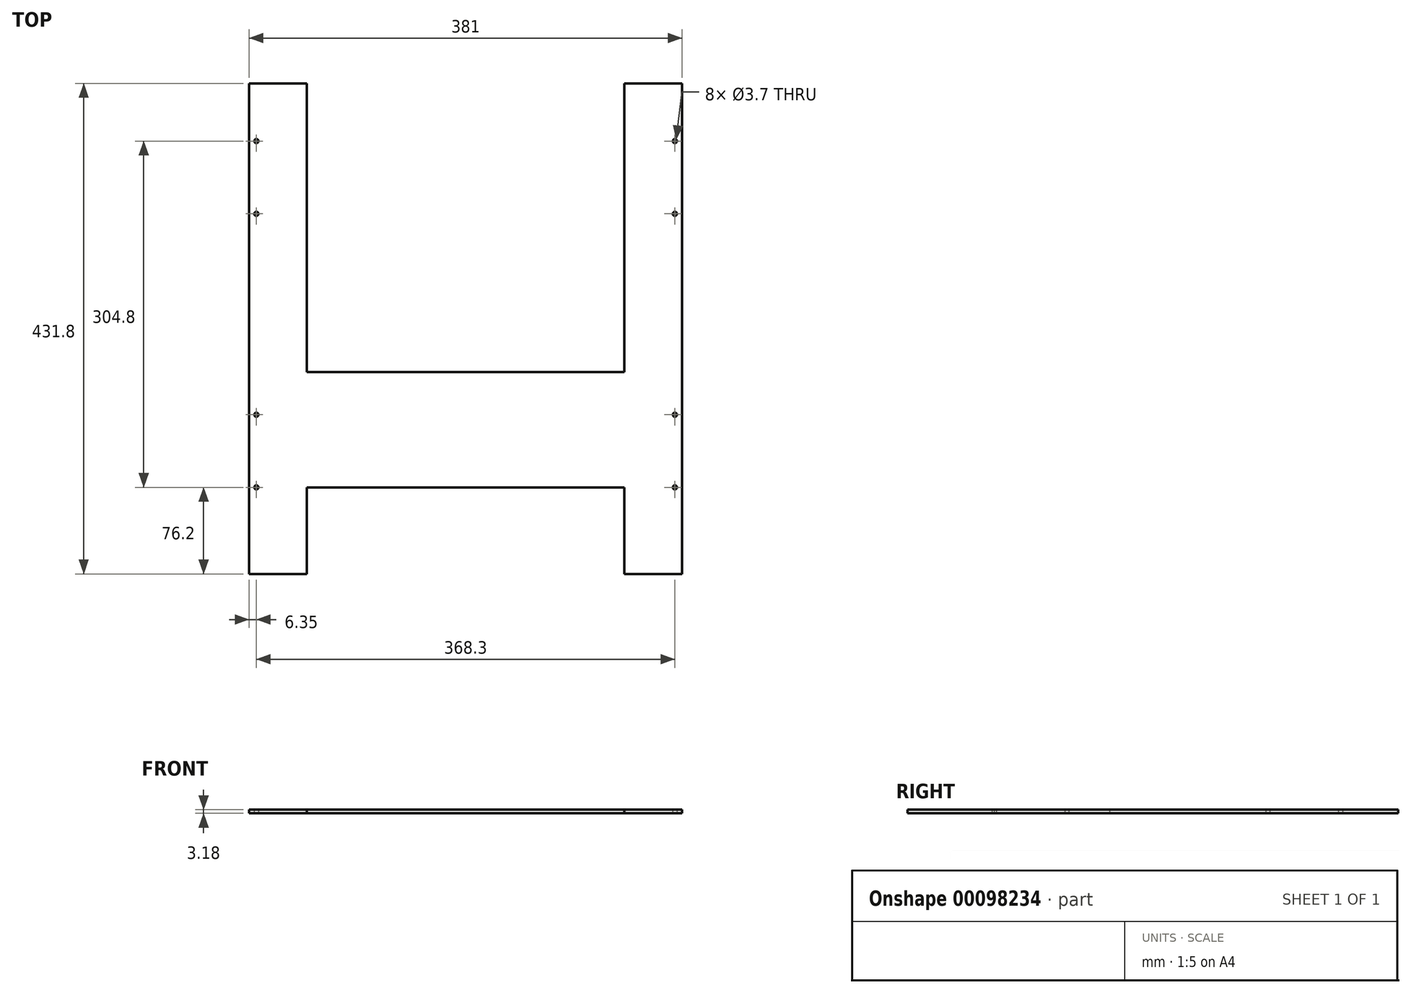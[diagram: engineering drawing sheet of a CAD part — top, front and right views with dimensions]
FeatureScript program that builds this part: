
annotation { "Feature Type Name" : "Feature", "Feature Type Description" : "" }
export const myFeature = defineFeature(function(context is Context, id is Id, definition is map)
    precondition{}
    {
        {
            var Q0;
            Q0=qCreatedBy(makeId("Top.planeOp"),FACE);
            var sketch = newSketch(context, id + "F0", { "sketchPlane" : qUnion([Q0])});
            skLineSegment(sketch, "E0.bottom", {"start": v(190.5, 215.9) * mm, "end": v(-190.5, 215.9) * mm});
            skLineSegment(sketch, "E0.top", {"start": v(190.5, -215.9) * mm, "end": v(-190.5, -215.9) * mm});
            skLineSegment(sketch, "E0.left", {"start": v(190.5, 215.9) * mm, "end": v(190.5, -215.9) * mm});
            skLineSegment(sketch, "E0.right", {"start": v(-190.5, 215.9) * mm, "end": v(-190.5, -215.9) * mm});
            skPoint(sketch, "E0.middle", {"position": v(0, 0) * mm});
            skPoint(sketch, "E1", {"position": v(-184.15, 165.1) * mm});
            skPoint(sketch, "E2", {"position": v(-184.15, 101.1) * mm});
            skPoint(sketch, "E3", {"position": v(-184.15, -75.7) * mm});
            skPoint(sketch, "E4", {"position": v(-184.15, -139.7) * mm});
            skPoint(sketch, "E5", {"position": v(184.15, -75.7) * mm});
            skPoint(sketch, "E6", {"position": v(184.15, -139.7) * mm});
            skPoint(sketch, "E7", {"position": v(184.15, 165.1) * mm});
            skPoint(sketch, "E8", {"position": v(184.15, 101.1) * mm});
            skCircle(sketch, "E9", {"center": v(-184.15, 165.1) * mm, "radius": 1.85 * mm});
            skCircle(sketch, "E10", {"center": v(-184.15, 101.1) * mm, "radius": 1.85 * mm});
            skCircle(sketch, "E11", {"center": v(-184.15, -75.7) * mm, "radius": 1.85 * mm});
            skCircle(sketch, "E12", {"center": v(-184.15, -139.7) * mm, "radius": 1.85 * mm});
            skCircle(sketch, "E13", {"center": v(184.15, -75.7) * mm, "radius": 1.85 * mm});
            skCircle(sketch, "E14", {"center": v(184.15, -139.7) * mm, "radius": 1.85 * mm});
            skCircle(sketch, "E15", {"center": v(184.15, 165.1) * mm, "radius": 1.85 * mm});
            skCircle(sketch, "E16", {"center": v(184.15, 101.1) * mm, "radius": 1.85 * mm});
            skLineSegment(sketch, "E17.bottom", {"start": v(-139.7, 215.9) * mm, "end": v(139.7, 215.9) * mm});
            skLineSegment(sketch, "E17.top", {"start": v(-139.7, -38.1) * mm, "end": v(139.7, -38.1) * mm});
            skLineSegment(sketch, "E17.left", {"start": v(-139.7, 215.9) * mm, "end": v(-139.7, -38.1) * mm});
            skLineSegment(sketch, "E17.right", {"start": v(139.7, 215.9) * mm, "end": v(139.7, -38.1) * mm});
            skLineSegment(sketch, "E18.bottom", {"start": v(-139.7, -139.7) * mm, "end": v(139.7, -139.7) * mm});
            skLineSegment(sketch, "E18.top", {"start": v(-139.7, -215.9) * mm, "end": v(139.7, -215.9) * mm});
            skLineSegment(sketch, "E18.left", {"start": v(-139.7, -139.7) * mm, "end": v(-139.7, -215.9) * mm});
            skLineSegment(sketch, "E18.right", {"start": v(139.7, -139.7) * mm, "end": v(139.7, -215.9) * mm});
            skSolve(sketch);
        }
        {
            var Q0;
            Q0=makeQuery(id+"F0.imprint","IMPRINT",FACE,{"disambiguationData":[TD([[makeQuery(id+"F0.imprint","IMPRINT",EDGE,{"derivedFrom":sQuery(id+"F0.wireOp",EDGE,"E0.bottom")}),1.0]])]});
            extrude(context, id + "F1", {"entities" : qUnion([Q0]), "depth" : 3.17 * mm});
        }
    });
